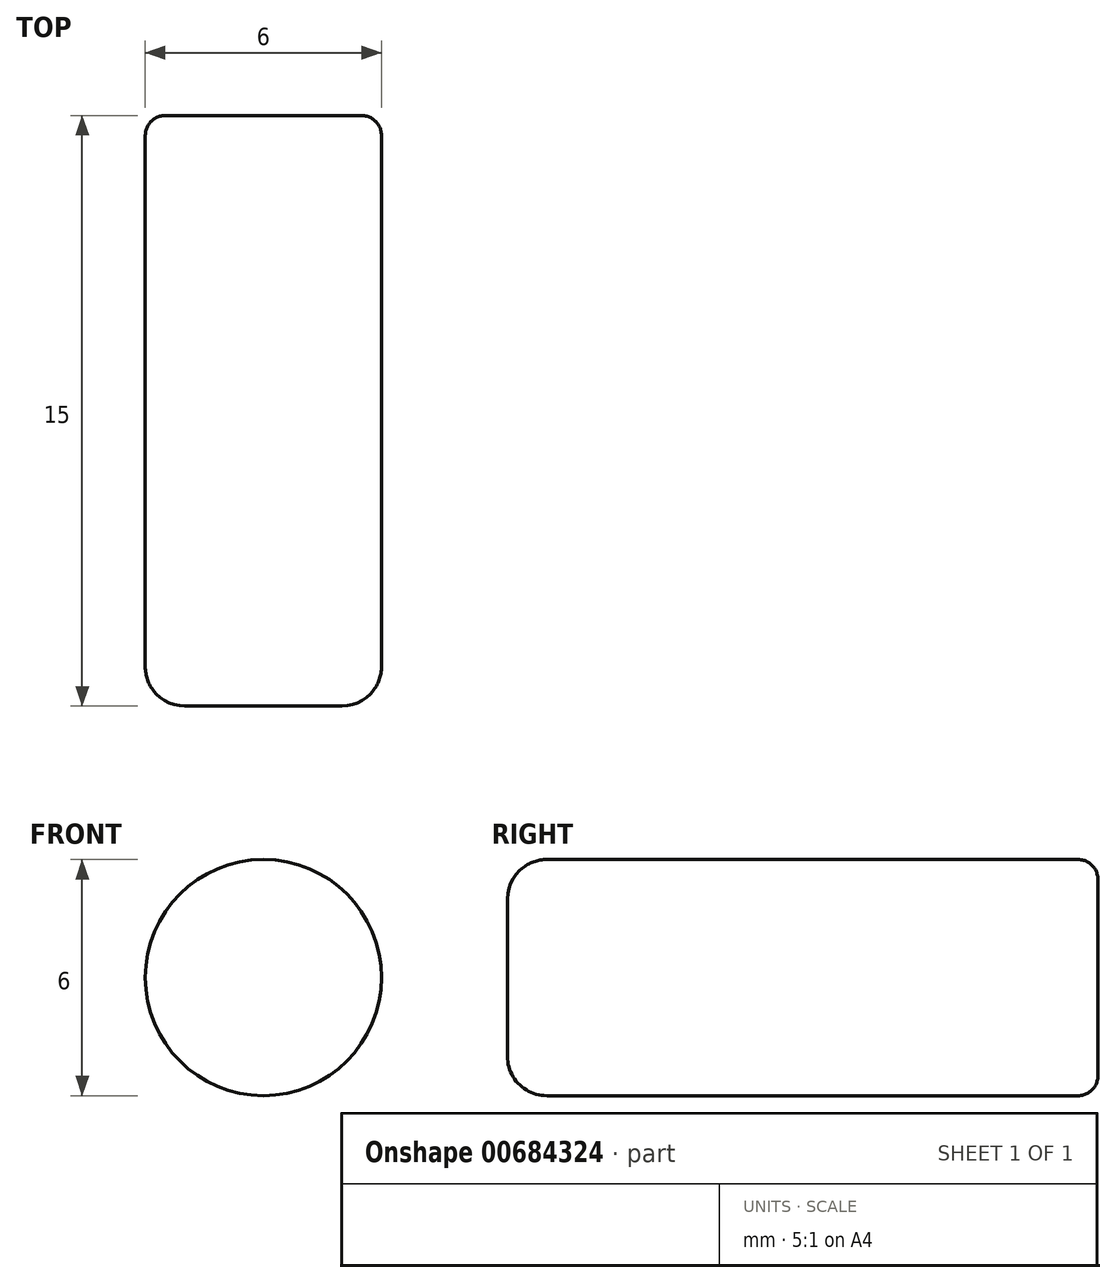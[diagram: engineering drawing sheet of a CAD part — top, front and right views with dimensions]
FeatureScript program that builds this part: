
annotation { "Feature Type Name" : "Feature", "Feature Type Description" : "" }
export const myFeature = defineFeature(function(context is Context, id is Id, definition is map)
    precondition{}
    {
        {
            var Q0;
            Q0=qCreatedBy(makeId("Front.planeOp"),FACE);
            var sketch = newSketch(context, id + "F0", { "sketchPlane" : qUnion([Q0])});
            skCircle(sketch, "E0", {"center": v(0, 0) * mm, "radius": 3 * mm});
            skSolve(sketch);
        }
        {
            var Q0;
            Q0 = qSketchRegion(id + "F0", true);
            extrude(context, id + "F1", {"entities" : qUnion([Q0]), "depth" : 15 * mm, "offsetDistance" : 25 * mm});
        }
        {
            var Q0;
            Q0=makeQuery(id+"F1.opExtrude","CAP_EDGE",EDGE,{"disambiguationData":[OSD([sQuery(id+"F0.wireOp",EDGE,"E0")])],"isStart":false});
            fillet(context, id + "F2", {"entities" : qUnion([Q0]), "radius" : 1 * mm, "tangentPropagation" : true, "allowEdgeOverflow" : false});
        }
        {
            var Q0;
            Q0=makeQuery(id+"F1.opExtrude","CAP_EDGE",EDGE,{"disambiguationData":[OSD([sQuery(id+"F0.wireOp",EDGE,"E0")])],"isStart":true});
            fillet(context, id + "F3", {"entities" : qUnion([Q0]), "radius" : .5 * mm, "tangentPropagation" : true, "allowEdgeOverflow" : false});
        }
    });
